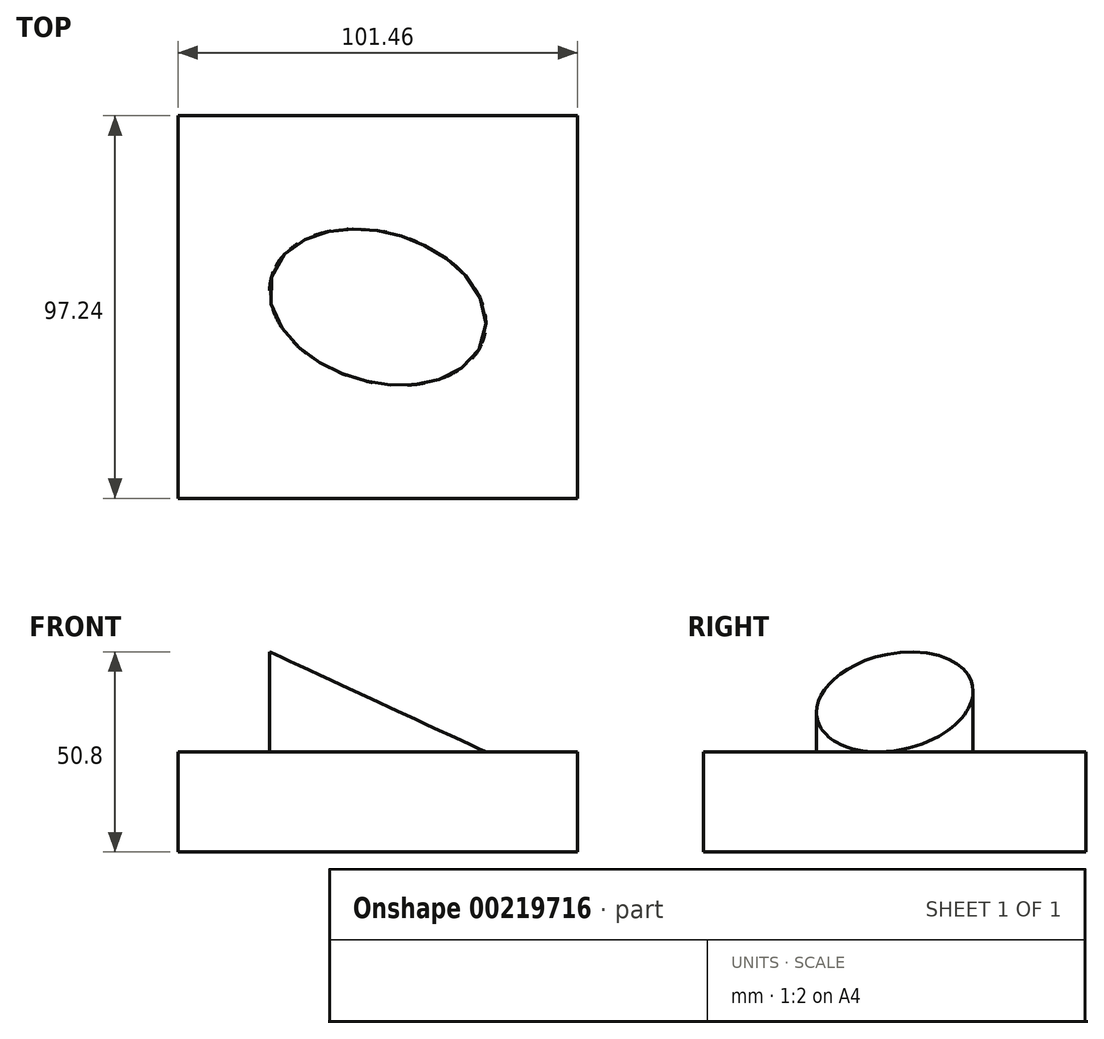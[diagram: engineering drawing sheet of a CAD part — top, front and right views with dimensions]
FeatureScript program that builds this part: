
annotation { "Feature Type Name" : "Feature", "Feature Type Description" : "" }
export const myFeature = defineFeature(function(context is Context, id is Id, definition is map)
    precondition{}
    {
        {
            var Q0;
            Q0=qCreatedBy(makeId("Top.planeOp"),FACE);
            var sketch = newSketch(context, id + "F0", { "sketchPlane" : qUnion([Q0])});
            skLineSegment(sketch, "E0.bottom", {"start": v(50.73, -48.62) * mm, "end": v(-50.73, -48.62) * mm});
            skLineSegment(sketch, "E0.top", {"start": v(50.73, 48.62) * mm, "end": v(-50.73, 48.62) * mm});
            skLineSegment(sketch, "E0.left", {"start": v(50.73, -48.62) * mm, "end": v(50.73, 48.62) * mm});
            skLineSegment(sketch, "E0.right", {"start": v(-50.73, -48.62) * mm, "end": v(-50.73, 48.62) * mm});
            skPoint(sketch, "E0.middle", {"position": v(0, 0) * mm});
            skSolve(sketch);
        }
        {
            var Q0;
            Q0=makeQuery(id+"F0.imprint","IMPRINT",FACE,{"disambiguationData":[TD([[makeQuery(id+"F0.imprint","IMPRINT",EDGE,{"derivedFrom":sQuery(id+"F0.wireOp",EDGE,"E0.bottom")}),-1.0]])]});
            extrude(context, id + "F1", {"entities" : qUnion([Q0]), "depth" : 25.4 * mm});
        }
        {
            var Q0;
            Q0=qCreatedBy(makeId("Top.planeOp"),FACE);
            var sketch = newSketch(context, id + "F2", { "sketchPlane" : qUnion([Q0])});
            skEllipse(sketch, "E1", {"center": v(0, 0) * mm, "majorRadius": 28.07 * mm, "minorRadius": 19 * mm, "majorAxis": v(0.96, -0.28)});
            skSolve(sketch);
        }
        {
            var Q0;
            Q0=makeQuery(id+"F2.imprint","IMPRINT",FACE,{"disambiguationData":[TD([[makeQuery(id+"F2.imprint","IMPRINT",EDGE,{"derivedFrom":sQuery(id+"F2.wireOp",EDGE,"E1")}),1.0]])]});
            var Q1;
            Q1=sQuery(id+"F2.wireOp",EDGE,"E1");
            extrude(context, id + "F3", {"entities" : qUnion([Q0]), "operationType" : NewBodyOperationType.ADD, "surfaceEntities" : qUnion([Q1]), "depth" : 50.8 * mm});
        }
        {
            var Q0;
            Q0=makeQuery(id+"F1.opExtrude","SWEPT_FACE",FACE,{"disambiguationData":[OSD([sQuery(id+"F0.wireOp",EDGE,"E0.bottom")])]});
            var sketch = newSketch(context, id + "F4", { "sketchPlane" : qUnion([Q0])});
            skLineSegment(sketch, "E2.0", {"start": v(-27.46, 50.8) * mm, "end": v(27.46, 50.8) * mm});
            skLineSegment(sketch, "E3", {"start": v(27.46, 50.8) * mm, "end": v(27.46, 25.4) * mm});
            skLineSegment(sketch, "E4", {"start": v(-27.46, 50.8) * mm, "end": v(27.46, 25.4) * mm});
            skSolve(sketch);
        }
        {
            var Q0;
            Q0 = qSketchRegion(id + "F4", true);
            extrude(context, id + "F5", {"entities" : qUnion([Q0]), "operationType" : NewBodyOperationType.REMOVE, "endBound" : BoundingType.THROUGH_ALL, "oppositeDirection" : true, "depth" : 25.4 * mm});
        }
    });
